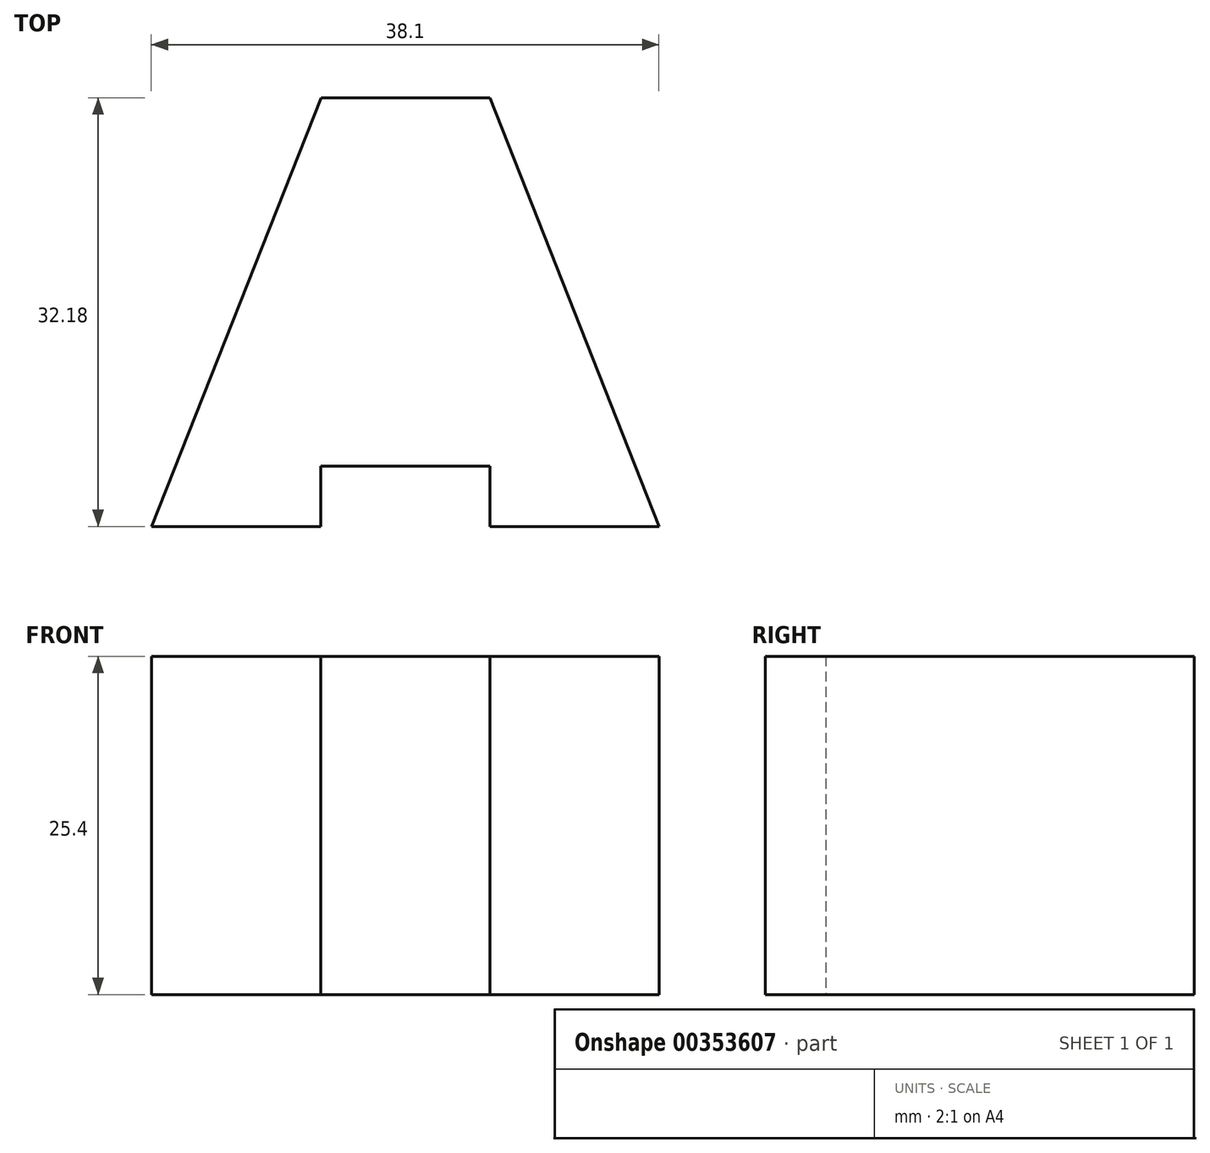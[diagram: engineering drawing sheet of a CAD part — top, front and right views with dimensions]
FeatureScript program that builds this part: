
annotation { "Feature Type Name" : "Feature", "Feature Type Description" : "" }
export const myFeature = defineFeature(function(context is Context, id is Id, definition is map)
    precondition{}
    {
        {
            var Q0;
            Q0=qCreatedBy(makeId("Top.planeOp"),FACE);
            var sketch = newSketch(context, id + "F0", { "sketchPlane" : qUnion([Q0])});
            skLineSegment(sketch, "E0", {"start": v(6.58, 0) * mm, "end": v(19.28, 0) * mm});
            skLineSegment(sketch, "E1", {"start": v(19.28, 0) * mm, "end": v(19.28, 4.54) * mm});
            skLineSegment(sketch, "E2", {"start": v(19.28, 4.54) * mm, "end": v(31.98, 4.54) * mm});
            skLineSegment(sketch, "E3", {"start": v(31.98, 4.54) * mm, "end": v(31.98, 0) * mm});
            skLineSegment(sketch, "E4", {"start": v(31.98, 0) * mm, "end": v(44.68, 0) * mm});
            skLineSegment(sketch, "E5", {"start": v(6.58, 0) * mm, "end": v(19.32, 32.18) * mm});
            skLineSegment(sketch, "E6", {"start": v(19.32, 32.18) * mm, "end": v(32.02, 32.18) * mm});
            skLineSegment(sketch, "E7", {"start": v(31.98, 32.18) * mm, "end": v(44.68, 0) * mm});
            skSolve(sketch);
        }
        {
            var Q0;
            Q0=makeQuery(id+"F0.imprint","IMPRINT",FACE,{"disambiguationData":[TD([[makeQuery(id+"F0.imprint","IMPRINT",EDGE,{"derivedFrom":sQuery(id+"F0.wireOp",EDGE,"E0")}),1.0]])]});
            extrude(context, id + "F1", {"entities" : qUnion([Q0]), "depth" : 25.4 * mm});
        }
    });
